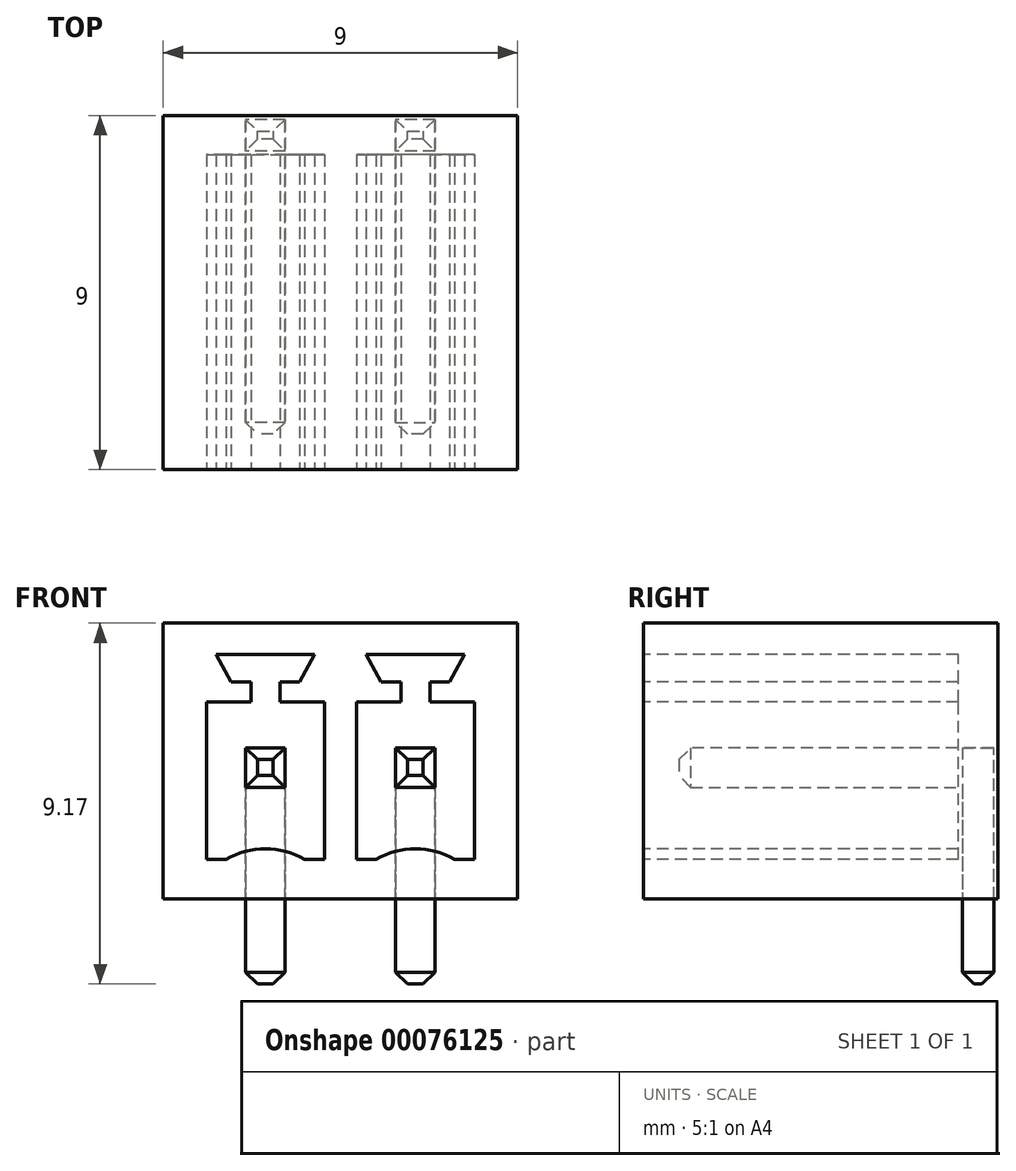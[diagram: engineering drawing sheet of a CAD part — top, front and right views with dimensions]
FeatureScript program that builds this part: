
annotation { "Feature Type Name" : "Feature", "Feature Type Description" : "" }
export const myFeature = defineFeature(function(context is Context, id is Id, definition is map)
    precondition{}
    {
        {
            var Q0;
            Q0=qCreatedBy(makeId("Top.planeOp"),FACE);
            var sketch = newSketch(context, id + "F0", { "sketchPlane" : qUnion([Q0])});
            skLineSegment(sketch, "E0.bottom", {"start": v(4.5, 4.5) * mm, "end": v(-4.5, 4.5) * mm});
            skLineSegment(sketch, "E0.top", {"start": v(4.5, -4.5) * mm, "end": v(-4.5, -4.5) * mm});
            skLineSegment(sketch, "E0.left", {"start": v(4.5, 4.5) * mm, "end": v(4.5, -4.5) * mm});
            skLineSegment(sketch, "E0.right", {"start": v(-4.5, 4.5) * mm, "end": v(-4.5, -4.5) * mm});
            skPoint(sketch, "E0.middle", {"position": v(0, 0) * mm});
            skSolve(sketch);
        }
        {
            var Q0;
            Q0=qSketchRegion(id+"F0",true);
            extrude(context, id + "F1", {"entities" : qUnion([Q0]), "depth" : 7 * mm});
        }
        {
            var Q0;
            Q0=makeQuery(id+"F1.opExtrude","SWEPT_FACE",FACE,{"disambiguationData":[OSD([sQuery(id+"F0.wireOp",EDGE,"E0.top")])]});
            var sketch = newSketch(context, id + "F2", { "sketchPlane" : qUnion([Q0])});
            skLineSegment(sketch, "E1", {"start": v(0, 0) * mm, "end": v(0, 7) * mm, "construction": true});
            skLineSegment(sketch, "E2", {"start": v(-0.4, 1) * mm, "end": v(-3.4, 1) * mm});
            skLineSegment(sketch, "E3", {"start": v(-3.4, 1) * mm, "end": v(-3.4, 5) * mm});
            skLineSegment(sketch, "E4", {"start": v(-3.4, 5) * mm, "end": v(-2.27, 5) * mm});
            skLineSegment(sketch, "E5", {"start": v(-2.27, 5) * mm, "end": v(-2.27, 5.5) * mm});
            skLineSegment(sketch, "E6", {"start": v(-2.27, 5.5) * mm, "end": v(-2.77, 5.5) * mm});
            skLineSegment(sketch, "E7", {"start": v(-2.77, 5.5) * mm, "end": v(-3.15, 6.2) * mm});
            skLineSegment(sketch, "E8", {"start": v(-3.15, 6.2) * mm, "end": v(-0.65, 6.2) * mm});
            skLineSegment(sketch, "E9", {"start": v(-0.66, 6.2) * mm, "end": v(-1.04, 5.5) * mm});
            skLineSegment(sketch, "E10", {"start": v(-1.04, 5.5) * mm, "end": v(-1.54, 5.5) * mm});
            skLineSegment(sketch, "E11", {"start": v(-1.54, 5.5) * mm, "end": v(-1.54, 5) * mm});
            skLineSegment(sketch, "E12", {"start": v(-1.54, 5) * mm, "end": v(-0.4, 5) * mm});
            skLineSegment(sketch, "E13", {"start": v(-0.4, 5) * mm, "end": v(-0.4, 1) * mm});
            skLineSegment(sketch, "E14", {"start": v(-1.9, 1) * mm, "end": v(-1.9, 6.2) * mm, "construction": true});
            skLineSegment(sketch, "E15.MirrorCS", {"start": v(0.66, 6.2) * mm, "end": v(1.04, 5.5) * mm});
            skLineSegment(sketch, "E16.MirrorCS", {"start": v(1.04, 5.5) * mm, "end": v(1.54, 5.5) * mm});
            skLineSegment(sketch, "E17.MirrorCS", {"start": v(1.54, 5.5) * mm, "end": v(1.54, 5) * mm});
            skLineSegment(sketch, "E18.MirrorCS", {"start": v(1.54, 5) * mm, "end": v(0.4, 5) * mm});
            skLineSegment(sketch, "E19.MirrorCS", {"start": v(2.27, 5) * mm, "end": v(2.27, 5.5) * mm});
            skLineSegment(sketch, "E20.MirrorCS", {"start": v(0.4, 5) * mm, "end": v(0.4, 1) * mm});
            skLineSegment(sketch, "E21.MirrorCS", {"start": v(3.4, 5) * mm, "end": v(2.27, 5) * mm});
            skLineSegment(sketch, "E22.MirrorCS", {"start": v(3.4, 1) * mm, "end": v(3.4, 5) * mm});
            skLineSegment(sketch, "E23.MirrorCS", {"start": v(0.4, 1) * mm, "end": v(3.4, 1) * mm});
            skLineSegment(sketch, "E24.MirrorCS", {"start": v(3.15, 6.2) * mm, "end": v(0.65, 6.2) * mm});
            skLineSegment(sketch, "E25.MirrorCS", {"start": v(2.27, 5.5) * mm, "end": v(2.77, 5.5) * mm});
            skLineSegment(sketch, "E26.MirrorCS", {"start": v(2.77, 5.5) * mm, "end": v(3.15, 6.2) * mm});
            skSolve(sketch);
        }
        {
            var Q0;
            Q0=qSketchRegion(id+"F2",true);
            extrude(context, id + "F3", {"entities" : qUnion([Q0]), "operationType" : NewBodyOperationType.REMOVE, "oppositeDirection" : true, "depth" : 8 * mm});
        }
        {
            var Q0;
            Q0=makeQuery(id+"F1.opExtrude","SWEPT_FACE",FACE,{"disambiguationData":[OSD([sQuery(id+"F0.wireOp",EDGE,"E0.bottom")])]});
            var sketch = newSketch(context, id + "F4", { "sketchPlane" : qUnion([Q0])});
            skLineSegment(sketch, "E27.bottom", {"start": v(-2.4, 3.84) * mm, "end": v(-1.4, 3.84) * mm});
            skLineSegment(sketch, "E27.top", {"start": v(-2.4, 0) * mm, "end": v(-1.4, 0) * mm});
            skLineSegment(sketch, "E27.left", {"start": v(-2.4, 3.84) * mm, "end": v(-2.4, 0) * mm});
            skLineSegment(sketch, "E27.right", {"start": v(-1.4, 3.84) * mm, "end": v(-1.4, 0) * mm});
            skLineSegment(sketch, "E28.bottom", {"start": v(1.4, 3.84) * mm, "end": v(2.4, 3.84) * mm});
            skLineSegment(sketch, "E28.top", {"start": v(1.4, 0) * mm, "end": v(2.4, 0) * mm});
            skLineSegment(sketch, "E28.left", {"start": v(1.4, 3.84) * mm, "end": v(1.4, 0) * mm});
            skLineSegment(sketch, "E28.right", {"start": v(2.4, 3.84) * mm, "end": v(2.4, 0) * mm});
            skPoint(sketch, "E29.centerSnap0", {"position": v(-1.9, 3.84) * mm});
            skPoint(sketch, "E30.centerSnap0", {"position": v(1.9, 3.84) * mm});
            skSolve(sketch);
        }
        {
            var Q0;
            {var subQ0=sQuery(id+"F4.wireOp",EDGE,"E27.top");Q0=makeQuery(id+"F4.imprint","IMPRINT",FACE,{"disambiguationData":[TD([[makeQuery(id+"F4.imprint","IMPRINT",EDGE,{"derivedFrom":subQ0}),1.0]])]});}
            var Q1;
            {var subQ0=sQuery(id+"F4.wireOp",EDGE,"E29");var subQ1=makeQuery(id+"F4.imprint","INTERSECT",VERTEX,{"derivedFrom":[sQuery(id+"F4.wireOp",EDGE,"E27.bottom"),subQ0]});Q1=makeQuery(id+"F4.imprint","IMPRINT",FACE,{"disambiguationData":[TD([[makeQuery(id+"F4.imprint","IMPRINT",EDGE,{"disambiguationData":[TD([[subQ1,1.0]])],"derivedFrom":subQ0}),1.0]])]});}
            var Q2;
            {var subQ0=sQuery(id+"F4.wireOp",EDGE,"E27.left");var subQ1=sQuery(id+"F4.wireOp",EDGE,"E27.bottom");var subQ2=makeQuery(id+"F4.imprint","INTERSECT",VERTEX,{"derivedFrom":[subQ1,subQ0]});Q2=makeQuery(id+"F4.imprint","IMPRINT",FACE,{"disambiguationData":[TD([[makeQuery(id+"F4.imprint","IMPRINT",EDGE,{"disambiguationData":[TD([[subQ2,-1.0]])],"derivedFrom":subQ1}),-1.0]])]});}
            var Q3;
            {var subQ0=sQuery(id+"F4.wireOp",EDGE,"E27.right");var subQ1=sQuery(id+"F4.wireOp",EDGE,"E27.bottom");var subQ2=makeQuery(id+"F4.imprint","INTERSECT",VERTEX,{"derivedFrom":[subQ1,subQ0]});Q3=makeQuery(id+"F4.imprint","IMPRINT",FACE,{"disambiguationData":[TD([[makeQuery(id+"F4.imprint","IMPRINT",EDGE,{"disambiguationData":[TD([[subQ2,1.0]])],"derivedFrom":subQ1}),-1.0]])]});}
            var Q4;
            {var subQ0=sQuery(id+"F4.wireOp",EDGE,"E28.top");Q4=makeQuery(id+"F4.imprint","IMPRINT",FACE,{"disambiguationData":[TD([[makeQuery(id+"F4.imprint","IMPRINT",EDGE,{"derivedFrom":subQ0}),1.0]])]});}
            var Q5;
            {var subQ0=sQuery(id+"F4.wireOp",EDGE,"E30");var subQ1=makeQuery(id+"F4.imprint","INTERSECT",VERTEX,{"derivedFrom":[sQuery(id+"F4.wireOp",EDGE,"E28.bottom"),subQ0]});Q5=makeQuery(id+"F4.imprint","IMPRINT",FACE,{"disambiguationData":[TD([[makeQuery(id+"F4.imprint","IMPRINT",EDGE,{"disambiguationData":[TD([[subQ1,1.0]])],"derivedFrom":subQ0}),1.0]])]});}
            var Q6;
            {var subQ0=sQuery(id+"F4.wireOp",EDGE,"E28.left");var subQ1=sQuery(id+"F4.wireOp",EDGE,"E28.bottom");var subQ2=makeQuery(id+"F4.imprint","INTERSECT",VERTEX,{"derivedFrom":[subQ1,subQ0]});Q6=makeQuery(id+"F4.imprint","IMPRINT",FACE,{"disambiguationData":[TD([[makeQuery(id+"F4.imprint","IMPRINT",EDGE,{"disambiguationData":[TD([[subQ2,-1.0]])],"derivedFrom":subQ1}),-1.0]])]});}
            var Q7;
            {var subQ0=sQuery(id+"F4.wireOp",EDGE,"E28.right");var subQ1=sQuery(id+"F4.wireOp",EDGE,"E28.bottom");var subQ2=makeQuery(id+"F4.imprint","INTERSECT",VERTEX,{"derivedFrom":[subQ1,subQ0]});Q7=makeQuery(id+"F4.imprint","IMPRINT",FACE,{"disambiguationData":[TD([[makeQuery(id+"F4.imprint","IMPRINT",EDGE,{"disambiguationData":[TD([[subQ2,1.0]])],"derivedFrom":subQ1}),-1.0]])]});}
            extrude(context, id + "F5", {"entities" : qUnion([Q0, Q1, Q2, Q3, Q4, Q5, Q6, Q7]), "operationType" : NewBodyOperationType.REMOVE, "oppositeDirection" : true, "depth" : 0.9 * mm});
        }
        {
            var Q0;
            Q0=qCreatedBy(makeId("Right.planeOp"),FACE);
            var sketch = newSketch(context, id + "F6", { "sketchPlane" : qUnion([Q0])});
            skLineSegment(sketch, "E31", {"start": v(4.4, -2.17) * mm, "end": v(4.4, 3.83) * mm});
            skLineSegment(sketch, "E32", {"start": v(4.4, 3.83) * mm, "end": v(-3.6, 3.83) * mm});
            skLineSegment(sketch, "E33", {"start": v(-3.6, 3.83) * mm, "end": v(-3.6, 2.83) * mm});
            skLineSegment(sketch, "E34", {"start": v(-3.6, 2.83) * mm, "end": v(3.6, 2.83) * mm});
            skLineSegment(sketch, "E35", {"start": v(3.6, 2.83) * mm, "end": v(3.6, -2.17) * mm});
            skLineSegment(sketch, "E36", {"start": v(3.6, -2.17) * mm, "end": v(4.4, -2.17) * mm});
            skSolve(sketch);
        }
        {
            var Q0;
            Q0=makeQuery(id+"F5.boolean.opBoolean","COPY",FACE,{"derivedFrom":makeQuery(id+"F5.opExtrude","SWEPT_FACE",FACE,{"disambiguationData":[OSD([sQuery(id+"F4.wireOp",EDGE,"E28.right")])]})});
            var sketch = newSketch(context, id + "F7", { "sketchPlane" : qUnion([Q0])});
            skLineSegment(sketch, "E37.0", {"start": v(-3.6, 3.83) * mm, "end": v(-3.6, 2.83) * mm});
            skLineSegment(sketch, "E38.0", {"start": v(4.4, 3.83) * mm, "end": v(-3.6, 3.83) * mm});
            skLineSegment(sketch, "E39.0", {"start": v(4.4, -2.17) * mm, "end": v(4.4, 3.83) * mm});
            skLineSegment(sketch, "E40.0", {"start": v(3.6, -2.17) * mm, "end": v(4.4, -2.17) * mm});
            skLineSegment(sketch, "E41.0", {"start": v(3.6, 2.83) * mm, "end": v(3.6, -2.17) * mm});
            skLineSegment(sketch, "E42.0", {"start": v(-3.6, 2.83) * mm, "end": v(3.6, 2.83) * mm});
            skSolve(sketch);
        }
        {
            var Q0;
            Q0=qSketchRegion(id+"F7",true);
            extrude(context, id + "F8", {"entities" : qUnion([Q0]), "depth" : 1 * mm});
        }
        {
            var Q0;
            Q0=makeQuery(id+"F5.boolean.opBoolean","COPY",FACE,{"derivedFrom":makeQuery(id+"F5.opExtrude","SWEPT_FACE",FACE,{"disambiguationData":[OSD([sQuery(id+"F4.wireOp",EDGE,"E27.right")])]})});
            var sketch = newSketch(context, id + "F9", { "sketchPlane" : qUnion([Q0])});
            skLineSegment(sketch, "E43.0", {"start": v(4.4, -2.17) * mm, "end": v(4.4, 3.83) * mm});
            skLineSegment(sketch, "E44.0", {"start": v(3.6, -2.17) * mm, "end": v(4.4, -2.17) * mm});
            skLineSegment(sketch, "E45.0", {"start": v(3.6, 2.83) * mm, "end": v(3.6, -2.17) * mm});
            skLineSegment(sketch, "E46.0", {"start": v(-3.6, 2.83) * mm, "end": v(3.6, 2.83) * mm});
            skLineSegment(sketch, "E47.0", {"start": v(-3.6, 3.83) * mm, "end": v(-3.6, 2.83) * mm});
            skLineSegment(sketch, "E48.0", {"start": v(4.4, 3.83) * mm, "end": v(-3.6, 3.83) * mm});
            skSolve(sketch);
        }
        {
            var Q0;
            Q0=qSketchRegion(id+"F9",true);
            extrude(context, id + "F10", {"entities" : qUnion([Q0]), "depth" : 1 * mm});
        }
        {
            var Q0;
            Q0=makeQuery(id+"F8.opExtrude","SWEPT_FACE",FACE,{"disambiguationData":[OSD([sQuery(id+"F7.wireOp",EDGE,"E37.0")])]});
            var Q1;
            Q1=makeQuery(id+"F10.opExtrude","SWEPT_FACE",FACE,{"disambiguationData":[OSD([sQuery(id+"F9.wireOp",EDGE,"E47.0")])]});
            var Q2;
            Q2=makeQuery(id+"F8.opExtrude","SWEPT_FACE",FACE,{"disambiguationData":[OSD([sQuery(id+"F7.wireOp",EDGE,"E40.0")])]});
            var Q3;
            Q3=makeQuery(id+"F10.opExtrude","SWEPT_FACE",FACE,{"disambiguationData":[OSD([sQuery(id+"F9.wireOp",EDGE,"E44.0")])]});
            chamfer(context, id + "F11", {"entities" : qUnion([Q0, Q1, Q2, Q3]), "width" : 0.3 * mm, "tangentPropagation" : true});
        }
        {
            var Q0;
            Q0=makeQuery(id+"F1.opExtrude","SWEPT_FACE",FACE,{"disambiguationData":[OSD([sQuery(id+"F0.wireOp",EDGE,"E0.top")])]});
            var sketch = newSketch(context, id + "F12", { "sketchPlane" : qUnion([Q0])});
            skArc(sketch, "E49", {"start": v(-0.9, 1) * mm, "mid": v(-1.9, 1.27) * mm, "end": v(-2.9, 1) * mm});
            skLineSegment(sketch, "E50", {"start": v(0, 7) * mm, "end": v(0, 0) * mm, "construction": true});
            skLineSegment(sketch, "E51", {"start": v(-2.9, 1) * mm, "end": v(-0.9, 1) * mm});
            skArc(sketch, "E52.MirrorCS", {"start": v(0.9, 1) * mm, "mid": v(1.9, 1.27) * mm, "end": v(2.9, 1) * mm});
            skLineSegment(sketch, "E53.MirrorCS", {"start": v(2.9, 1) * mm, "end": v(0.9, 1) * mm});
            skSolve(sketch);
        }
        {
            var Q0;
            Q0=qSketchRegion(id+"F12",true);
            var Q1;
            Q1=makeQuery(id+"F3.boolean.opBoolean","COPY",FACE,{"derivedFrom":makeQuery(id+"F3.opExtrude","CAP_FACE",FACE,{"disambiguationData":[OSD([sQuery(id+"F2.wireOp",EDGE,"E2"),sQuery(id+"F2.wireOp",EDGE,"E3"),sQuery(id+"F2.wireOp",EDGE,"E4"),sQuery(id+"F2.wireOp",EDGE,"E5"),sQuery(id+"F2.wireOp",EDGE,"E6"),sQuery(id+"F2.wireOp",EDGE,"E7"),sQuery(id+"F2.wireOp",EDGE,"E8"),sQuery(id+"F2.wireOp",EDGE,"E9"),sQuery(id+"F2.wireOp",EDGE,"E10"),sQuery(id+"F2.wireOp",EDGE,"E11"),sQuery(id+"F2.wireOp",EDGE,"E12"),sQuery(id+"F2.wireOp",EDGE,"E13")])],"isStart":false})});
            extrude(context, id + "F13", {"entities" : qUnion([Q0]), "operationType" : NewBodyOperationType.ADD, "endBound" : BoundingType.UP_TO_SURFACE, "oppositeDirection" : true, "endBoundEntityFace" : qUnion([Q1]), "depth" : 25 * mm});
        }
    });
